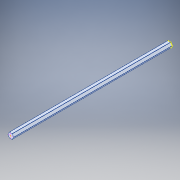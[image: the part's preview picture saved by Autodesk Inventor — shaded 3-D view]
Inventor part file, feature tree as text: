
AUTODESK INVENTOR PART (.ipt)
format: ipt  version: 2017 (Build 210142000, 142)  size: 160,768 bytes
history: native  units: in
note: dims shown in document units (in); Inventor stores cm internally (conversion verified against a paired STEP export)
features: sketch x7, split x1, projected_geometry x1, fillet x1
ambient origin geometry x8: Origin, YZ Plane, XZ Plane, XY Plane, X Axis, Y Axis, Z Axis, Center Point
bodies: Solid1 (feature_tree)
feature tree (10):
  sketch  "Sketch1"  dims[d11=16.0in]
  split  "Split1"
  sketch  "Sketch3"  dims[d13=7.8125in]
  sketch  "Sketch4"  dims[d14=3.5453in]
  sketch  "Sketch5"  dims[d15=3.5453in]
  sketch  "Sketch7"
  sketch  "Sketch8"
  sketch  "Sketch2"  dims[d12=7.8125in]
  projected_geometry  "Projected Loop1"
  fillet  "Fillet1"  Radius=8.5in
